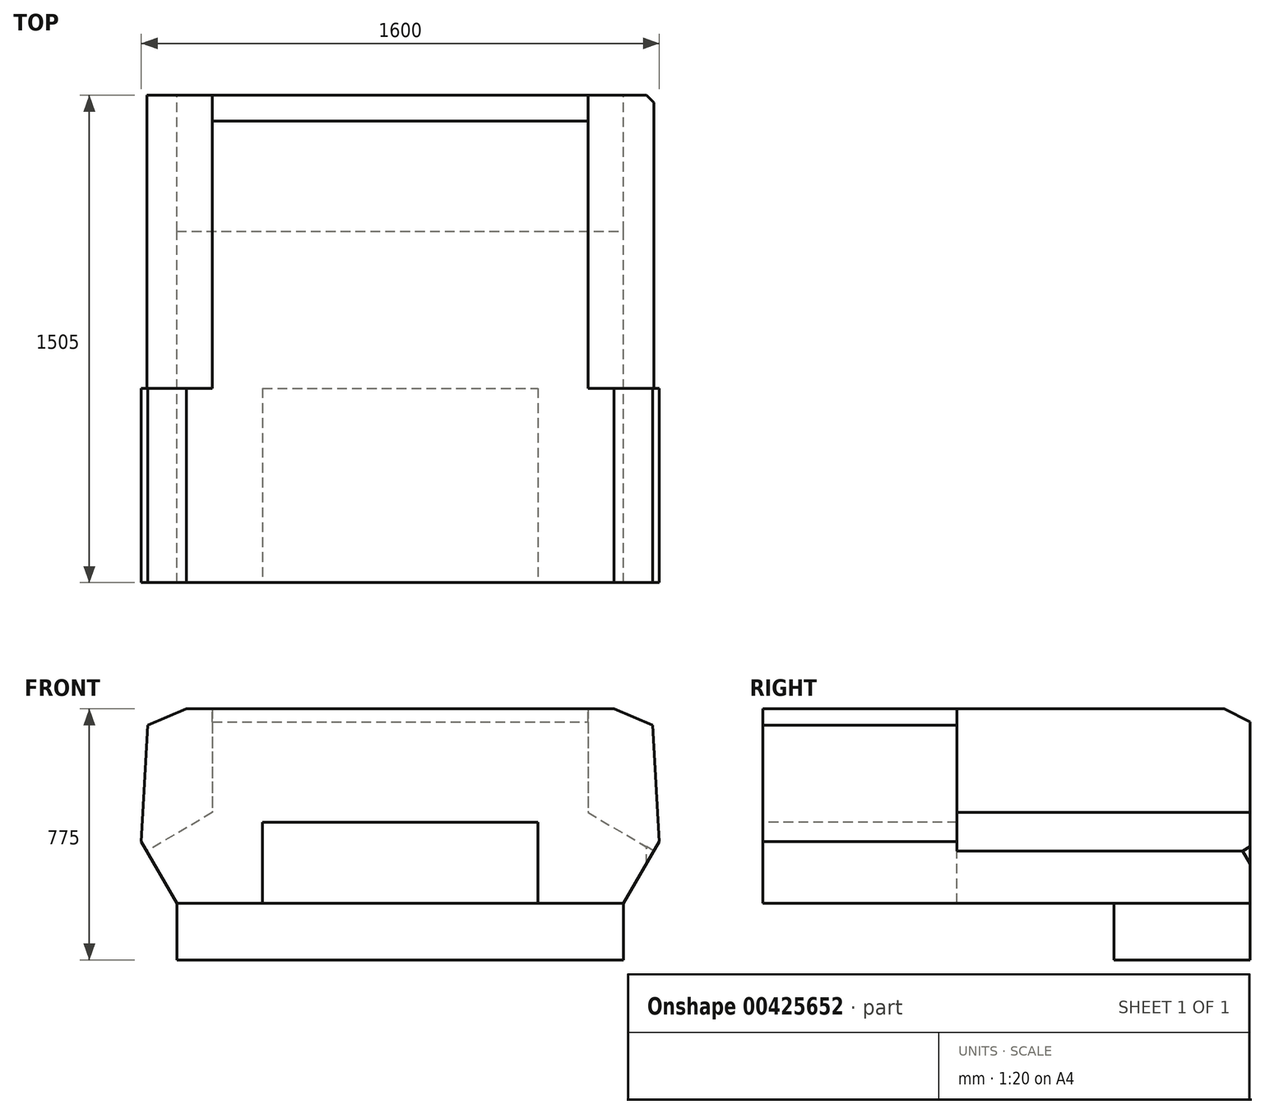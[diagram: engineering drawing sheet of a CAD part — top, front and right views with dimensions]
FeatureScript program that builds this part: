
annotation { "Feature Type Name" : "Feature", "Feature Type Description" : "" }
export const myFeature = defineFeature(function(context is Context, id is Id, definition is map)
    precondition{}
    {
        {
            var Q0;
            Q0=qCreatedBy(makeId("Front.planeOp"),FACE);
            var sketch = newSketch(context, id + "F0", { "sketchPlane" : qUnion([Q0])});
            skLineSegment(sketch, "E0", {"start": v(-624.66, 0) * mm, "end": v(755.34, 0) * mm});
            skLineSegment(sketch, "E1", {"start": v(755.34, 0) * mm, "end": v(865.34, 190.53) * mm});
            skLineSegment(sketch, "E2", {"start": v(865.34, 190.53) * mm, "end": v(845.34, 550) * mm});
            skLineSegment(sketch, "E3", {"start": v(845.34, 550) * mm, "end": v(725.34, 600) * mm});
            skLineSegment(sketch, "E4", {"start": v(725.34, 600) * mm, "end": v(-594.66, 600) * mm});
            skLineSegment(sketch, "E5", {"start": v(-594.66, 600) * mm, "end": v(-714.66, 550) * mm});
            skLineSegment(sketch, "E6", {"start": v(-714.66, 550) * mm, "end": v(-734.66, 190.53) * mm});
            skLineSegment(sketch, "E7", {"start": v(-734.66, 190.53) * mm, "end": v(-624.66, 0) * mm});
            skSolve(sketch);
        }
        {
            var Q0;
            Q0=makeQuery(id+"F0.imprint","IMPRINT",FACE,{"disambiguationData":[TD([[makeQuery(id+"F0.imprint","IMPRINT",EDGE,{"derivedFrom":sQuery(id+"F0.wireOp",EDGE,"E0")}),1.0]])]});
            extrude(context, id + "F1", {"entities" : qUnion([Q0]), "depth" : 1505 * mm});
        }
        {
            var Q0;
            Q0=qCreatedBy(makeId("Right.planeOp"),FACE);
            var sketch = newSketch(context, id + "F2", { "sketchPlane" : qUnion([Q0])});
            skLineSegment(sketch, "E8", {"start": v(-80, 600) * mm, "end": v(0, 560) * mm});
            skLineSegment(sketch, "E9", {"start": v(0, 560) * mm, "end": v(0, 600) * mm});
            skLineSegment(sketch, "E10", {"start": v(0, 600) * mm, "end": v(-80, 600) * mm});
            skSolve(sketch);
        }
        {
            var Q0;
            Q0=qSketchRegion(id+"F2",true);
            extrude(context, id + "F3", {"entities" : qUnion([Q0]), "operationType" : NewBodyOperationType.REMOVE, "endBound" : BoundingType.THROUGH_ALL, "oppositeDirection" : true, "depth" : 25 * mm, "hasSecondDirection" : true, "secondDirectionBound" : SecondDirectionBoundingType.THROUGH_ALL, "secondDirectionOppositeDirection" : false, "secondDirectionDepth" : 25 * mm});
        }
        {
            var Q0;
            Q0=makeQuery(id+"F1.opExtrude","SWEPT_FACE",FACE,{"disambiguationData":[OSD([sQuery(id+"F0.wireOp",EDGE,"E4")])]});
            var sketch = newSketch(context, id + "F4", { "sketchPlane" : qUnion([Q0])});
            skLineSegment(sketch, "E11", {"start": v(825.34, 0) * mm, "end": v(865.34, -40) * mm});
            skLineSegment(sketch, "E12", {"start": v(865.34, -40) * mm, "end": v(865.34, 0) * mm});
            skLineSegment(sketch, "E13", {"start": v(865.34, 0) * mm, "end": v(825.34, 0) * mm});
            skSolve(sketch);
        }
        {
            var Q0;
            Q0=makeQuery(id+"F4.imprint","IMPRINT",FACE,{"disambiguationData":[TD([[makeQuery(id+"F4.imprint","IMPRINT",EDGE,{"derivedFrom":sQuery(id+"F4.wireOp",EDGE,"E11")}),1.0]])]});
            extrude(context, id + "F5", {"entities" : qUnion([Q0]), "operationType" : NewBodyOperationType.REMOVE, "endBound" : BoundingType.THROUGH_ALL, "oppositeDirection" : true, "depth" : 25 * mm});
        }
        {
            var Q0;
            Q0=makeQuery(id+"F1.opExtrude","CAP_FACE",FACE,{"disambiguationData":[OSD([sQuery(id+"F0.wireOp",EDGE,"E0"),sQuery(id+"F0.wireOp",EDGE,"E1"),sQuery(id+"F0.wireOp",EDGE,"E2"),sQuery(id+"F0.wireOp",EDGE,"E3"),sQuery(id+"F0.wireOp",EDGE,"E4"),sQuery(id+"F0.wireOp",EDGE,"E5"),sQuery(id+"F0.wireOp",EDGE,"E6"),sQuery(id+"F0.wireOp",EDGE,"E7")])],"isStart":false});
            var sketch = newSketch(context, id + "F6", { "sketchPlane" : qUnion([Q0])});
            skLineSegment(sketch, "E14.bottom", {"start": v(-359.66, 0) * mm, "end": v(490.34, 0) * mm});
            skLineSegment(sketch, "E14.top", {"start": v(-359.66, 250) * mm, "end": v(490.34, 250) * mm});
            skLineSegment(sketch, "E14.left", {"start": v(-359.66, 0) * mm, "end": v(-359.66, 250) * mm});
            skLineSegment(sketch, "E14.right", {"start": v(490.34, 0) * mm, "end": v(490.34, 250) * mm});
            skLineSegment(sketch, "E15", {"start": v(65.34, 250) * mm, "end": v(65.34, 0) * mm, "construction": true});
            skSolve(sketch);
        }
        {
            var Q0;
            Q0=makeQuery(id+"F6.imprint","IMPRINT",FACE,{"disambiguationData":[TD([[makeQuery(id+"F6.imprint","IMPRINT",EDGE,{"derivedFrom":sQuery(id+"F6.wireOp",EDGE,"E14.bottom")}),1.0]])]});
            extrude(context, id + "F7", {"entities" : qUnion([Q0]), "operationType" : NewBodyOperationType.REMOVE, "oppositeDirection" : true, "depth" : 600 * mm});
        }
        {
            var Q0;
            Q0=makeQuery(id+"F1.opExtrude","CAP_FACE",FACE,{"disambiguationData":[OSD([sQuery(id+"F0.wireOp",EDGE,"E0"),sQuery(id+"F0.wireOp",EDGE,"E1"),sQuery(id+"F0.wireOp",EDGE,"E2"),sQuery(id+"F0.wireOp",EDGE,"E3"),sQuery(id+"F0.wireOp",EDGE,"E4"),sQuery(id+"F0.wireOp",EDGE,"E5"),sQuery(id+"F0.wireOp",EDGE,"E6"),sQuery(id+"F0.wireOp",EDGE,"E7")])],"isStart":true});
            var sketch = newSketch(context, id + "F8", { "sketchPlane" : qUnion([Q0])});
            skLineSegment(sketch, "E16", {"start": v(514.66, 280) * mm, "end": v(717.61, 161) * mm});
            skLineSegment(sketch, "E17", {"start": v(717.61, 161) * mm, "end": v(734.66, 190.53) * mm});
            skLineSegment(sketch, "E18", {"start": v(734.66, 190.53) * mm, "end": v(714.66, 550) * mm});
            skLineSegment(sketch, "E19", {"start": v(714.66, 550) * mm, "end": v(594.66, 600) * mm});
            skLineSegment(sketch, "E20", {"start": v(594.66, 600) * mm, "end": v(514.66, 600) * mm});
            skLineSegment(sketch, "E21", {"start": v(514.66, 600) * mm, "end": v(514.66, 280) * mm});
            skLineSegment(sketch, "E22", {"start": v(-65.34, 674.16) * mm, "end": v(-65.34, -176.75) * mm, "construction": true});
            skLineSegment(sketch, "E23.MirrorCS", {"start": v(-848.3, 161) * mm, "end": v(-865.34, 190.53) * mm});
            skLineSegment(sketch, "E24.MirrorCS", {"start": v(-645.34, 600) * mm, "end": v(-645.34, 280) * mm});
            skLineSegment(sketch, "E25.MirrorCS", {"start": v(-725.34, 600) * mm, "end": v(-645.34, 600) * mm});
            skLineSegment(sketch, "E26.MirrorCS", {"start": v(-845.34, 550) * mm, "end": v(-725.34, 600) * mm});
            skLineSegment(sketch, "E27.MirrorCS", {"start": v(-865.34, 190.53) * mm, "end": v(-845.34, 550) * mm});
            skLineSegment(sketch, "E28.MirrorCS", {"start": v(-645.34, 280) * mm, "end": v(-848.3, 161) * mm});
            skSolve(sketch);
        }
        {
            var Q0;
            {var subQ3=sQuery(id+"F8.wireOp",EDGE,"E20");Q0=makeQuery(id+"F8.imprint","IMPRINT",FACE,{"disambiguationData":[TD([[makeQuery(id+"F8.imprint","IMPRINT",EDGE,{"derivedFrom":subQ3}),1.0]])]});}
            var Q1;
            {var subQ4=sQuery(id+"F8.wireOp",EDGE,"E16");Q1=makeQuery(id+"F8.imprint","IMPRINT",FACE,{"disambiguationData":[TD([[makeQuery(id+"F8.imprint","IMPRINT",EDGE,{"derivedFrom":subQ4}),1.0]])]});}
            var Q2;
            {var subQ3=sQuery(id+"F8.wireOp",EDGE,"E24.MirrorCS");var subQ5=sQuery(id+"F8.wireOp",EDGE,"E28.MirrorCS");var subQ6=makeQuery(id+"F8.imprint","INTERSECT",VERTEX,{"derivedFrom":[subQ3,subQ5]});Q2=makeQuery(id+"F8.imprint","IMPRINT",FACE,{"disambiguationData":[TD([[makeQuery(id+"F8.imprint","IMPRINT",EDGE,{"disambiguationData":[TD([[subQ6,1.0]])],"derivedFrom":subQ3}),-1.0]])]});}
            var Q3;
            {var subQ0=sQuery(id+"F8.wireOp",EDGE,"E25.MirrorCS");Q3=makeQuery(id+"F8.imprint","IMPRINT",FACE,{"disambiguationData":[TD([[makeQuery(id+"F8.imprint","IMPRINT",EDGE,{"derivedFrom":subQ0}),-1.0]])]});}
            var Q4;
            {var subQ2=sQuery(id+"F8.wireOp",EDGE,"E23.MirrorCS");Q4=makeQuery(id+"F8.imprint","IMPRINT",FACE,{"disambiguationData":[TD([[makeQuery(id+"F8.imprint","IMPRINT",EDGE,{"derivedFrom":subQ2}),-1.0]])]});}
            extrude(context, id + "F9", {"entities" : qUnion([Q0, Q1, Q2, Q3, Q4]), "operationType" : NewBodyOperationType.REMOVE, "oppositeDirection" : true, "depth" : 905 * mm});
        }
        {
            var Q0;
            Q0=makeQuery(id+"F1.opExtrude","CAP_FACE",FACE,{"disambiguationData":[OSD([sQuery(id+"F0.wireOp",EDGE,"E0"),sQuery(id+"F0.wireOp",EDGE,"E1"),sQuery(id+"F0.wireOp",EDGE,"E2"),sQuery(id+"F0.wireOp",EDGE,"E3"),sQuery(id+"F0.wireOp",EDGE,"E4"),sQuery(id+"F0.wireOp",EDGE,"E5"),sQuery(id+"F0.wireOp",EDGE,"E6"),sQuery(id+"F0.wireOp",EDGE,"E7")])],"isStart":true});
            var sketch = newSketch(context, id + "F10", { "sketchPlane" : qUnion([Q0])});
            skLineSegment(sketch, "E29.bottom", {"start": v(-755.34, 0) * mm, "end": v(624.66, 0) * mm});
            skLineSegment(sketch, "E29.top", {"start": v(-755.34, -175) * mm, "end": v(624.66, -175) * mm});
            skLineSegment(sketch, "E29.left", {"start": v(-755.34, 0) * mm, "end": v(-755.34, -175) * mm});
            skLineSegment(sketch, "E29.right", {"start": v(624.66, 0) * mm, "end": v(624.66, -175) * mm});
            skSolve(sketch);
        }
        {
            var Q0;
            Q0=makeQuery(id+"F10.imprint","IMPRINT",FACE,{"disambiguationData":[TD([[makeQuery(id+"F10.imprint","IMPRINT",EDGE,{"derivedFrom":sQuery(id+"F10.wireOp",EDGE,"E29.bottom")}),1.0]])]});
            extrude(context, id + "F11", {"entities" : qUnion([Q0]), "operationType" : NewBodyOperationType.ADD, "oppositeDirection" : true, "depth" : 420 * mm});
        }
    });
